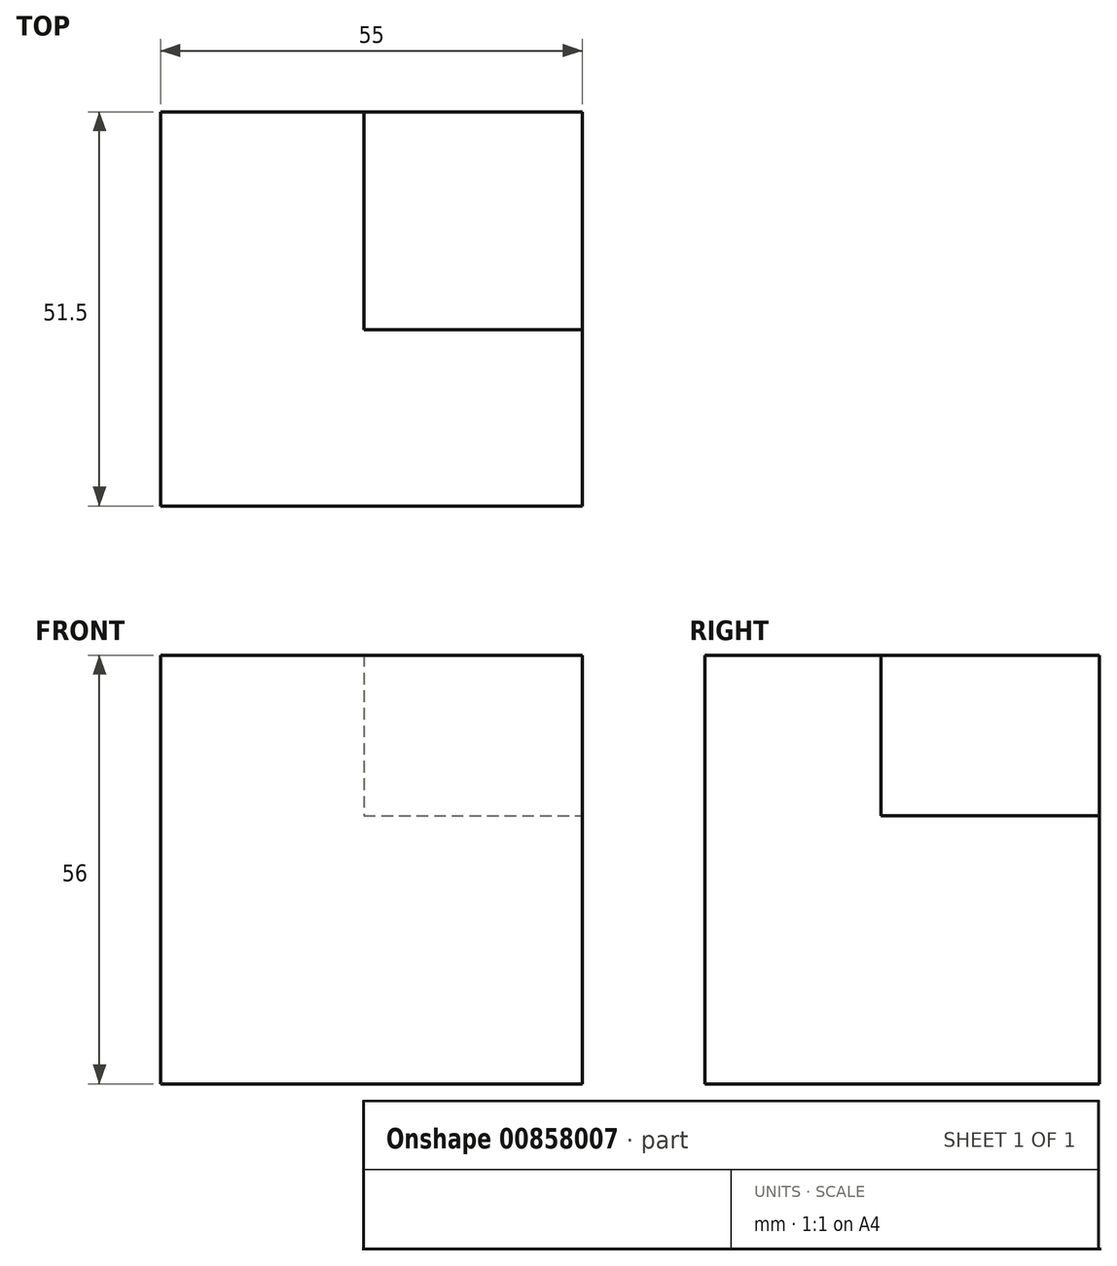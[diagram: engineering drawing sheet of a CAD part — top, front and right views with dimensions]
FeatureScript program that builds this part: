
annotation { "Feature Type Name" : "Feature", "Feature Type Description" : "" }
export const myFeature = defineFeature(function(context is Context, id is Id, definition is map)
    precondition{}
    {
        {
            var Q0;
            Q0=qCreatedBy(makeId("Top.planeOp"),FACE);
            var sketch = newSketch(context, id + "F0", { "sketchPlane" : qUnion([Q0])});
            skLineSegment(sketch, "E0", {"start": v(-27.34, 25.9) * mm, "end": v(27.66, 25.9) * mm});
            skLineSegment(sketch, "E1", {"start": v(27.66, 25.9) * mm, "end": v(27.66, -25.6) * mm});
            skLineSegment(sketch, "E2", {"start": v(27.66, -25.6) * mm, "end": v(-27.34, -25.6) * mm});
            skLineSegment(sketch, "E3", {"start": v(-27.34, -25.6) * mm, "end": v(-27.34, 25.9) * mm});
            skLineSegment(sketch, "E4", {"start": v(27.66, 25.9) * mm, "end": v(-27.34, -25.6) * mm});
            skSolve(sketch);
        }
        {
            var Q0;
            Q0 = qSketchRegion(id + "F0", true);
            extrude(context, id + "F1", {"entities" : qUnion([Q0]), "depth" : 35 * mm, "offsetDistance" : 25 * mm});
        }
        {
            var Q0;
            Q0=makeQuery(id+"F1.opExtrude","CAP_FACE",FACE,{"disambiguationData":[OSD([sQuery(id+"F0.wireOp",EDGE,"E0"),sQuery(id+"F0.wireOp",EDGE,"E1"),sQuery(id+"F0.wireOp",EDGE,"E2"),sQuery(id+"F0.wireOp",EDGE,"E3")])],"isStart":false});
            var sketch = newSketch(context, id + "F2", { "sketchPlane" : qUnion([Q0])});
            skLineSegment(sketch, "E5", {"start": v(-27.34, 25.9) * mm, "end": v(-27.34, -25.6) * mm});
            skLineSegment(sketch, "E6", {"start": v(-27.34, -25.6) * mm, "end": v(27.66, -25.6) * mm});
            skLineSegment(sketch, "E7", {"start": v(27.66, -25.6) * mm, "end": v(27.66, -2.6) * mm});
            skLineSegment(sketch, "E8", {"start": v(27.66, -2.6) * mm, "end": v(-0.84, -2.6) * mm});
            skLineSegment(sketch, "E9", {"start": v(-0.84, -2.6) * mm, "end": v(-0.84, 25.9) * mm});
            skLineSegment(sketch, "E10", {"start": v(-0.84, 25.9) * mm, "end": v(-27.34, 25.9) * mm});
            skSolve(sketch);
        }
        {
            var Q0;
            Q0 = qSketchRegion(id + "F2", true);
            extrude(context, id + "F3", {"entities" : qUnion([Q0]), "operationType" : NewBodyOperationType.ADD, "depth" : 21 * mm, "offsetDistance" : 25 * mm});
        }
    });
